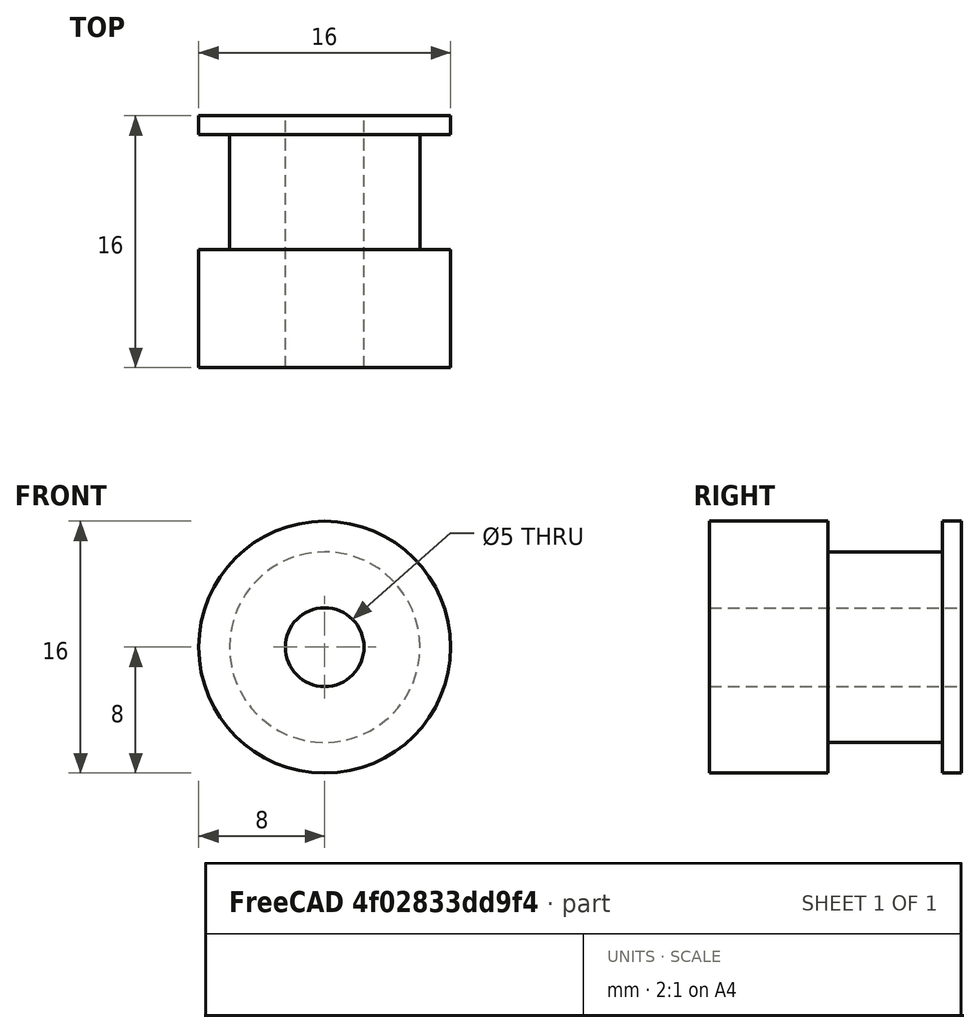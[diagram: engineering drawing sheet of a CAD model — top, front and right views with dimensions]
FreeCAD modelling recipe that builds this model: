
FCSTD DOCUMENT  (FreeCAD 0.17R12560 (Git))
Label: timing_pulley_gt2_20T_bore_5
License: All rights reserved
LicenseURL: http://en.wikipedia.org/wiki/All_rights_reserved
objects: Sketcher::SketchObject×1, PartDesign::Revolution×1
note: 3 computed .brp shape members not serialized (recipe doc carries the construction recipe); baked Part::Feature solids carry a one-line shape summary decoded from their .brp

FEATURE [Sketcher::SketchObject] Sketch
  MapMode = 5
  sketch-geometry (9):
    g0: LineSegment StartX=2.5 StartY=0 StartZ=0 EndX=2.5 EndY=16 EndZ=0
    g1: LineSegment StartX=2.5 StartY=16 StartZ=0 EndX=8 EndY=16 EndZ=0
    g2: LineSegment StartX=8 StartY=7.5 StartZ=0 EndX=8 EndY=0 EndZ=0
    g3: LineSegment StartX=8 StartY=0 StartZ=0 EndX=2.5 EndY=0 EndZ=0
    g4: LineSegment StartX=8 StartY=7.5 StartZ=0 EndX=6.05 EndY=7.5 EndZ=0
    g5: LineSegment StartX=6.05 StartY=7.5 StartZ=0 EndX=6.05 EndY=14.8 EndZ=0
    g6: LineSegment StartX=6.05 StartY=14.8 StartZ=0 EndX=8 EndY=14.8 EndZ=0
    g7: LineSegment StartX=8 StartY=14.8 StartZ=0 EndX=8 EndY=16 EndZ=0
    g8: LineSegment [constr] StartX=8 StartY=7.5 StartZ=0 EndX=8 EndY=14.8 EndZ=0
  constraints (26):
    c: Vertical(g0)
    c: Coincident(g0,g1)
    c: Horizontal(g1)
    c: Vertical(g2)
    c: Coincident(g2,g3)
    c: Coincident(g3,g0)
    c: Horizontal(g3)
    c: DistanceY(g0,g0) = 16
    c: PointOnObject(g0,g-1)
    c: DistanceX(g-1,g2) = 8
    c: DistanceX(g-1,g0) = 2.5
    c: DistanceY(g2) = -7.5
    c: Horizontal(g4)
    c: Coincident(g4,g5)
    c: Vertical(g5)
    c: Coincident(g5,g6)
    c: Horizontal(g6)
    c: Coincident(g6,g7)
    c: Coincident(g7,g1)
    c: Vertical(g7)
    c: Coincident(g8,g6)
    c: Vertical(g8)
    c: Coincident(g4,g8)
    c: Coincident(g4,g2)
    c: DistanceY(g8) = 7.3
    c: DistanceX(g-1,g5) = 6.05
FEATURE [PartDesign::Revolution] Revolution
  Angle = 360
  Axis = (0,1,0)
  Base = (0,0,0)
  Profile = -> Sketch
  ReferenceAxis = -> Sketch [V_Axis]
  Reversed = true
